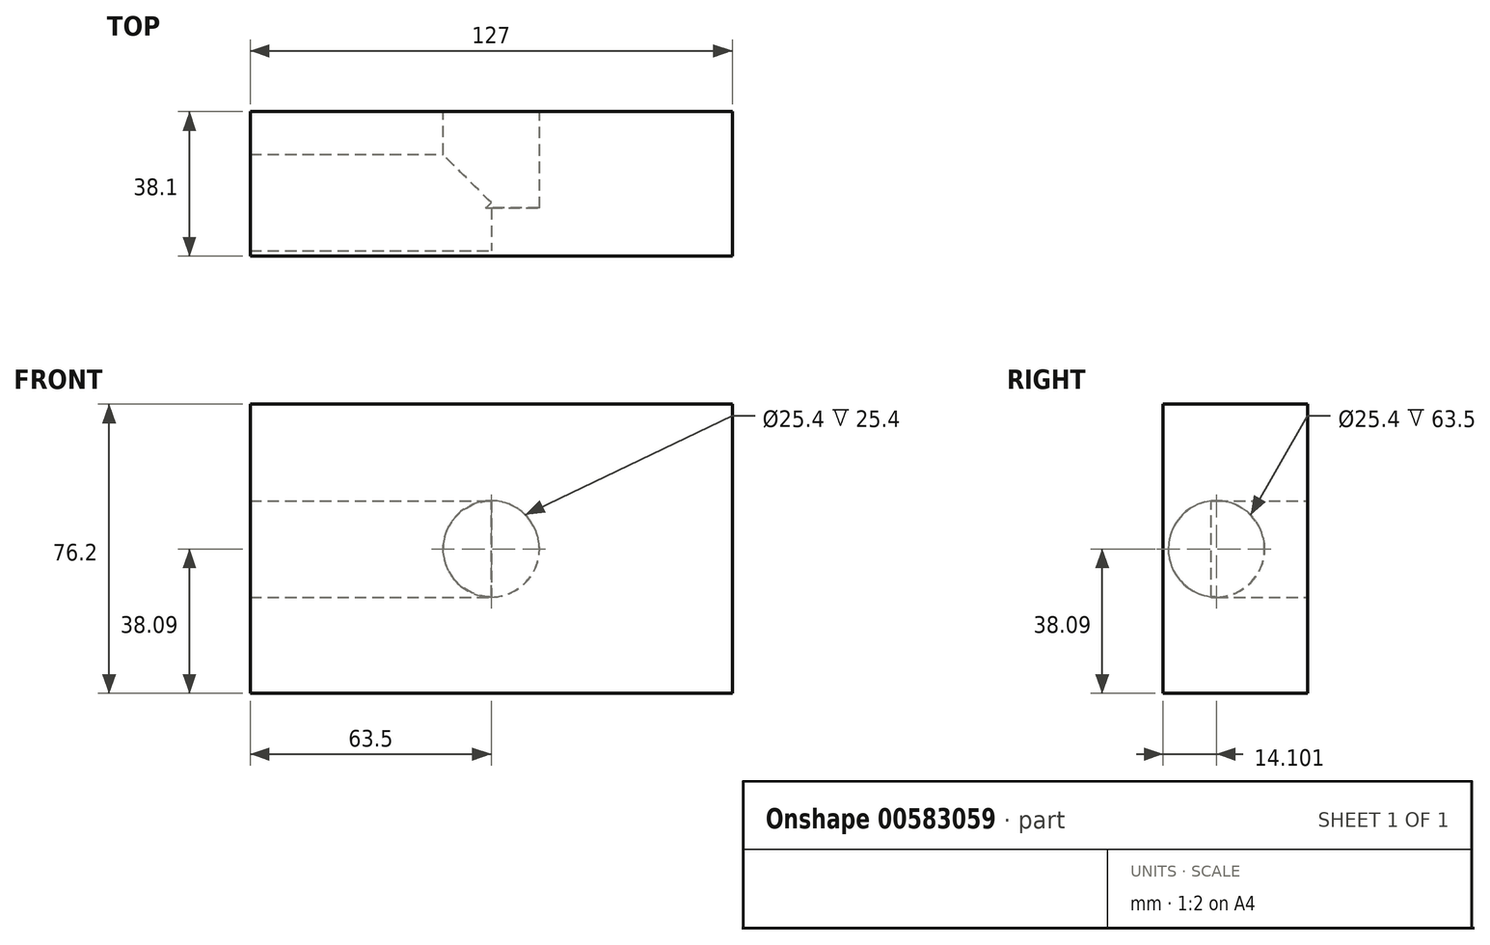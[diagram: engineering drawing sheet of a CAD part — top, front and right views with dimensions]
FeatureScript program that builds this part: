
annotation { "Feature Type Name" : "Feature", "Feature Type Description" : "" }
export const myFeature = defineFeature(function(context is Context, id is Id, definition is map)
    precondition{}
    {
        {
            var Q0;
            Q0=qCreatedBy(makeId("Front.planeOp"),FACE);
            var sketch = newSketch(context, id + "F0", { "sketchPlane" : qUnion([Q0])});
            skLineSegment(sketch, "E0.bottom", {"start": v(-63.5, 38.11) * mm, "end": v(63.5, 38.11) * mm});
            skLineSegment(sketch, "E0.top", {"start": v(-63.5, -38.09) * mm, "end": v(63.5, -38.09) * mm});
            skLineSegment(sketch, "E0.left", {"start": v(-63.5, 38.11) * mm, "end": v(-63.5, -38.09) * mm});
            skLineSegment(sketch, "E0.right", {"start": v(63.5, 38.11) * mm, "end": v(63.5, -38.09) * mm});
            skSolve(sketch);
        }
        {
            var Q0;
            Q0=qCreatedBy(makeId("Front.planeOp"),FACE);
            var sketch = newSketch(context, id + "F1", { "sketchPlane" : qUnion([Q0])});
            skCircle(sketch, "E1", {"center": v(0, 0) * mm, "radius": 12.7 * mm});
            skSolve(sketch);
        }
        {
            var Q0;
            Q0=makeQuery(id+"F0.imprint","IMPRINT",FACE,{"disambiguationData":[TD([[makeQuery(id+"F0.imprint","IMPRINT",EDGE,{"derivedFrom":sQuery(id+"F0.wireOp",EDGE,"E0.bottom")}),-1.0]])]});
            extrude(context, id + "F2", {"entities" : qUnion([Q0]), "depth" : 38.1 * mm, "offsetDistance" : 25.4 * mm});
        }
        {
            var Q0;
            Q0 = qSketchRegion(id + "F1", true);
            extrude(context, id + "F3", {"entities" : qUnion([Q0]), "operationType" : NewBodyOperationType.REMOVE, "depth" : 25.4 * mm, "offsetDistance" : 25.4 * mm});
        }
        {
            var Q0;
            Q0=qCreatedBy(makeId("Right.planeOp"),FACE);
            var sketch = newSketch(context, id + "F4", { "sketchPlane" : qUnion([Q0])});
            skCircle(sketch, "E2", {"center": v(-24, 0) * mm, "radius": 12.7 * mm});
            skSolve(sketch);
        }
        {
            var Q0;
            Q0 = qSketchRegion(id + "F4", true);
            extrude(context, id + "F5", {"entities" : qUnion([Q0]), "operationType" : NewBodyOperationType.REMOVE, "oppositeDirection" : true, "depth" : 76.2 * mm, "offsetDistance" : 25.4 * mm});
        }
    });
